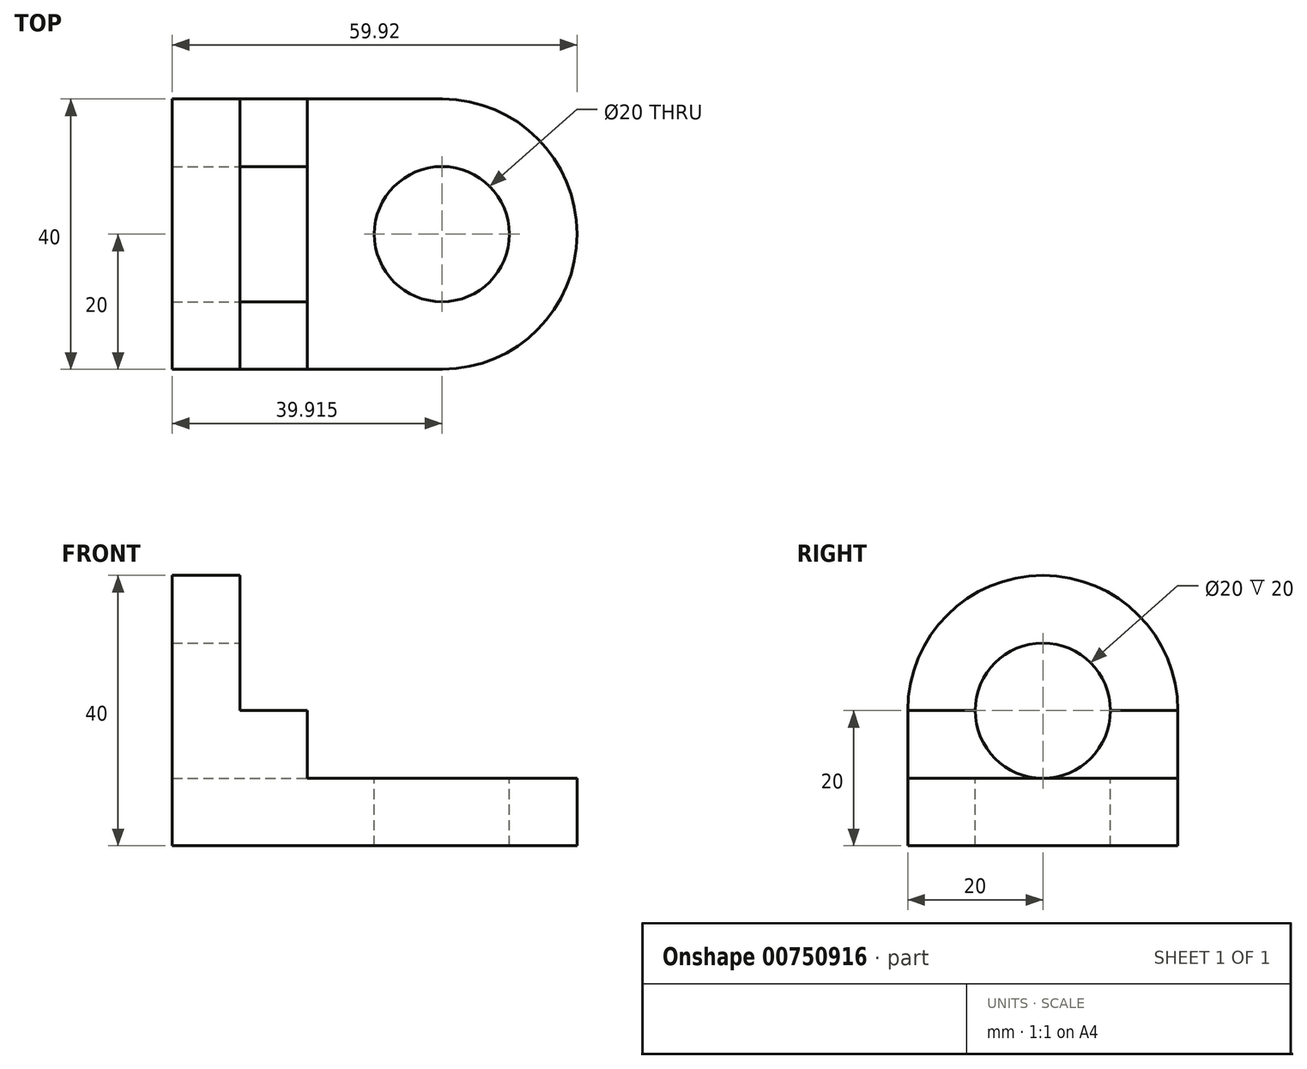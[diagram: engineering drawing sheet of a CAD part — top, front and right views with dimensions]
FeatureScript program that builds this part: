
annotation { "Feature Type Name" : "Feature", "Feature Type Description" : "" }
export const myFeature = defineFeature(function(context is Context, id is Id, definition is map)
    precondition{}
    {
        {
            var Q0;
            Q0=qCreatedBy(makeId("Front.planeOp"),FACE);
            var sketch = newSketch(context, id + "F0", { "sketchPlane" : qUnion([Q0])});
            skLineSegment(sketch, "E0", {"start": v(0, 0) * mm, "end": v(60, 0) * mm});
            skLineSegment(sketch, "E1", {"start": v(60, 0) * mm, "end": v(60, 10) * mm});
            skLineSegment(sketch, "E2", {"start": v(60, 10) * mm, "end": v(20, 10) * mm});
            skLineSegment(sketch, "E3", {"start": v(20, 10) * mm, "end": v(20, 20) * mm});
            skLineSegment(sketch, "E4", {"start": v(20, 20) * mm, "end": v(10, 20) * mm});
            skLineSegment(sketch, "E5", {"start": v(10, 20) * mm, "end": v(10, 40) * mm});
            skLineSegment(sketch, "E6", {"start": v(10, 40) * mm, "end": v(0, 40) * mm});
            skLineSegment(sketch, "E7", {"start": v(0, 40) * mm, "end": v(0, 0) * mm});
            skSolve(sketch);
        }
        {
            var Q0;
            Q0=makeQuery(id+"F0.imprint","IMPRINT",FACE,{"disambiguationData":[TD([[makeQuery(id+"F0.imprint","IMPRINT",EDGE,{"derivedFrom":sQuery(id+"F0.wireOp",EDGE,"E0")}),1.0]])]});
            extrude(context, id + "F1", {"entities" : qUnion([Q0]), "depth" : 40 * mm, "offsetDistance" : 25 * mm});
        }
        {
            var Q0;
            Q0=makeQuery(id+"F1.opExtrude","SWEPT_FACE",FACE,{"disambiguationData":[OSD([sQuery(id+"F0.wireOp",EDGE,"E3")])]});
            var sketch = newSketch(context, id + "F2", { "sketchPlane" : qUnion([Q0])});
            skCircle(sketch, "E8", {"center": v(-20, 20) * mm, "radius": 10 * mm});
            skSolve(sketch);
        }
        {
            var Q0;
            {var subQ0=sQuery(id+"F2.wireOp",EDGE,"E8");var subQ1=makeQuery(id+"F1.opExtrude","SWEPT_EDGE",EDGE,{"disambiguationData":[OSD([sQuery(id+"F0.wireOp",EDGE,"E3"),sQuery(id+"F0.wireOp",EDGE,"E4")])]});var subQ2=makeQuery(id+"F2.imprint","INTERSECT",VERTEX,{"disambiguationData":[OD(0.0)],"derivedFrom":[subQ1,subQ0]});Q0=makeQuery(id+"F2.imprint","IMPRINT",FACE,{"disambiguationData":[TD([[makeQuery(id+"F2.imprint","IMPRINT",EDGE,{"disambiguationData":[TD([[subQ2,1.0]])],"derivedFrom":subQ0}),1.0]])]});}
            var Q1;
            {var subQ0=sQuery(id+"F2.wireOp",EDGE,"E8");var subQ1=sQuery(id+"F0.wireOp",EDGE,"E3");var subQ2=makeQuery(id+"F1.opExtrude","SWEPT_EDGE",EDGE,{"disambiguationData":[OSD([subQ1,sQuery(id+"F0.wireOp",EDGE,"E4")])]});var subQ3=makeQuery(id+"F2.imprint","INTERSECT",VERTEX,{"disambiguationData":[OD(0.0)],"derivedFrom":[subQ2,subQ0]});Q1=makeQuery(id+"F2.imprint","IMPRINT",FACE,{"disambiguationData":[TD([[makeQuery(id+"F2.imprint","IMPRINT",EDGE,{"disambiguationData":[TD([[subQ3,-1.0]])],"derivedFrom":subQ0}),1.0]])]});}
            extrude(context, id + "F3", {"entities" : qUnion([Q0, Q1]), "operationType" : NewBodyOperationType.REMOVE, "oppositeDirection" : true, "depth" : 20 * mm, "offsetDistance" : 25 * mm});
        }
        {
            var Q0;
            Q0=makeQuery(id+"F1.opExtrude","SWEPT_FACE",FACE,{"disambiguationData":[OSD([sQuery(id+"F0.wireOp",EDGE,"E5")])]});
            var sketch = newSketch(context, id + "F4", { "sketchPlane" : qUnion([Q0])});
            skArc(sketch, "E9", {"start": v(0, 20) * mm, "mid": v(-20, 40) * mm, "end": v(-40, 20) * mm});
            skSolve(sketch);
        }
        {
            var Q0;
            {var subQ2=sQuery(id+"F0.wireOp",EDGE,"E5");var subQ4=makeQuery(id+"F1.opExtrude","CAP_EDGE",EDGE,{"disambiguationData":[OSD([subQ2])],"isStart":false});Q0=makeQuery(id+"F4.imprint","IMPRINT",FACE,{"disambiguationData":[TD([[makeQuery(id+"F4.imprint","IMPRINT",EDGE,{"derivedFrom":subQ4}),-1.0]])]});}
            var Q1;
            {var subQ2=sQuery(id+"F0.wireOp",EDGE,"E5");var subQ4=makeQuery(id+"F1.opExtrude","CAP_EDGE",EDGE,{"disambiguationData":[OSD([subQ2])],"isStart":true});Q1=makeQuery(id+"F4.imprint","IMPRINT",FACE,{"disambiguationData":[TD([[makeQuery(id+"F4.imprint","IMPRINT",EDGE,{"derivedFrom":subQ4}),1.0]])]});}
            extrude(context, id + "F5", {"entities" : qUnion([Q0, Q1]), "operationType" : NewBodyOperationType.REMOVE, "oppositeDirection" : true, "depth" : 20 * mm, "offsetDistance" : 25 * mm});
        }
        {
            var Q0;
            Q0=makeQuery(id+"F1.opExtrude","SWEPT_FACE",FACE,{"disambiguationData":[OSD([sQuery(id+"F0.wireOp",EDGE,"E2")])]});
            var sketch = newSketch(context, id + "F6", { "sketchPlane" : qUnion([Q0])});
            skArc(sketch, "E10", {"start": v(40, -40) * mm, "mid": v(59.92, -20) * mm, "end": v(40, 0) * mm});
            skSolve(sketch);
        }
        {
            var Q0;
            {var subQ0=sQuery(id+"F6.wireOp",EDGE,"E10");Q0=makeQuery(id+"F6.imprint","IMPRINT",FACE,{"disambiguationData":[TD([[makeQuery(id+"F6.imprint","IMPRINT",EDGE,{"derivedFrom":subQ0}),-1.0]])]});}
            extrude(context, id + "F7", {"entities" : qUnion([Q0]), "operationType" : NewBodyOperationType.REMOVE, "oppositeDirection" : true, "depth" : 10 * mm, "offsetDistance" : 25 * mm});
        }
        {
            var Q0;
            Q0=makeQuery(id+"F1.opExtrude","SWEPT_FACE",FACE,{"disambiguationData":[OSD([sQuery(id+"F0.wireOp",EDGE,"E2")])]});
            var sketch = newSketch(context, id + "F8", { "sketchPlane" : qUnion([Q0])});
            skCircle(sketch, "E11", {"center": v(39.92, -20) * mm, "radius": 10 * mm});
            skSolve(sketch);
        }
        {
            var Q0;
            Q0=makeQuery(id+"F8.imprint","IMPRINT",FACE,{"disambiguationData":[TD([[makeQuery(id+"F8.imprint","IMPRINT",EDGE,{"derivedFrom":sQuery(id+"F8.wireOp",EDGE,"E11")}),1.0]])]});
            extrude(context, id + "F9", {"entities" : qUnion([Q0]), "operationType" : NewBodyOperationType.REMOVE, "oppositeDirection" : true, "depth" : 10 * mm, "offsetDistance" : 25 * mm});
        }
    });
